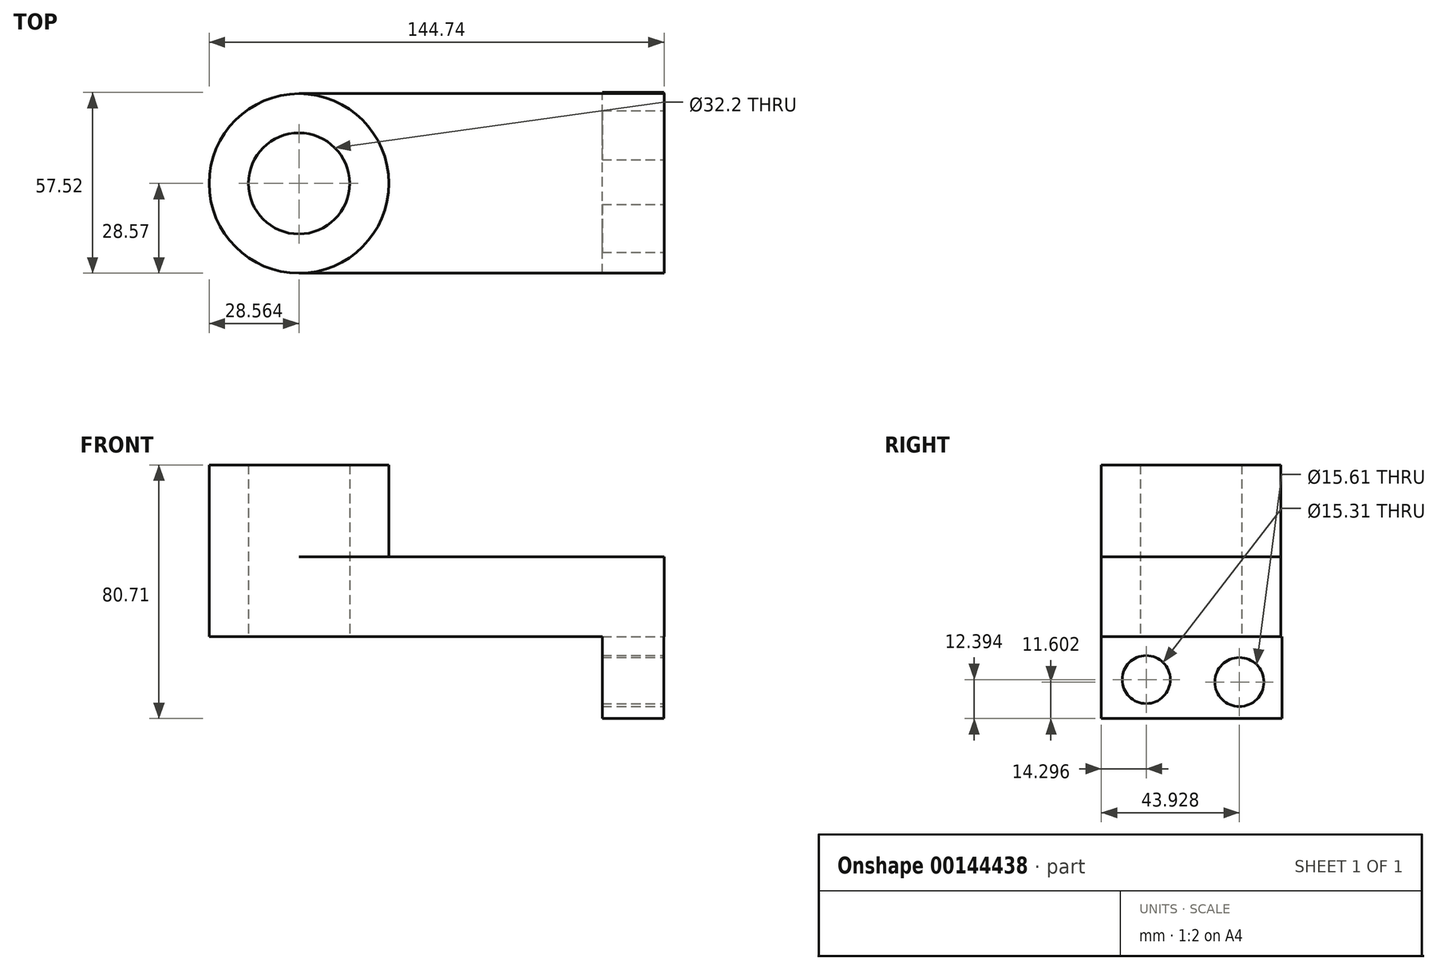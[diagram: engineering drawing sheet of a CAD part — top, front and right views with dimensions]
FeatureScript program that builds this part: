
annotation { "Feature Type Name" : "Feature", "Feature Type Description" : "" }
export const myFeature = defineFeature(function(context is Context, id is Id, definition is map)
    precondition{}
    {
        {
            var Q0;
            Q0=qCreatedBy(makeId("Top.planeOp"),FACE);
            var sketch = newSketch(context, id + "F0", { "sketchPlane" : qUnion([Q0])});
            skLineSegment(sketch, "E0.bottom", {"start": v(-58.09, 28.57) * mm, "end": v(58.09, 28.57) * mm});
            skLineSegment(sketch, "E0.top", {"start": v(-58.09, -28.57) * mm, "end": v(58.09, -28.57) * mm});
            skLineSegment(sketch, "E0.left", {"start": v(-58.09, 28.57) * mm, "end": v(-58.09, -28.57) * mm});
            skLineSegment(sketch, "E0.right", {"start": v(58.09, 28.57) * mm, "end": v(58.09, -28.57) * mm});
            skPoint(sketch, "E0.middle", {"position": v(0, 0) * mm});
            skCircle(sketch, "E1", {"center": v(-58.09, 0) * mm, "radius": 28.57 * mm});
            skCircle(sketch, "E2", {"center": v(-58.09, 0) * mm, "radius": 16.1 * mm});
            skSolve(sketch);
        }
        {
            var Q0;
            {var subQ1=sQuery(id+"F0.wireOp",EDGE,"E0.left");var subQ3=sQuery(id+"F0.wireOp",EDGE,"E2");var subQ4=makeQuery(id+"F0.imprint","INTERSECT",VERTEX,{"disambiguationData":[OD(0.0)],"derivedFrom":[subQ1,subQ3]});Q0=makeQuery(id+"F0.imprint","IMPRINT",FACE,{"disambiguationData":[TD([[makeQuery(id+"F0.imprint","IMPRINT",EDGE,{"disambiguationData":[TD([[subQ4,-1.0]])],"derivedFrom":subQ3}),-1.0]])]});}
            var Q1;
            {var subQ1=sQuery(id+"F0.wireOp",EDGE,"E0.left");var subQ3=sQuery(id+"F0.wireOp",EDGE,"E2");var subQ4=makeQuery(id+"F0.imprint","INTERSECT",VERTEX,{"disambiguationData":[OD(0.0)],"derivedFrom":[subQ1,subQ3]});Q1=makeQuery(id+"F0.imprint","IMPRINT",FACE,{"disambiguationData":[TD([[makeQuery(id+"F0.imprint","IMPRINT",EDGE,{"disambiguationData":[TD([[subQ4,1.0]])],"derivedFrom":subQ3}),-1.0]])]});}
            var Q2;
            {var subQ0=sQuery(id+"F0.wireOp",EDGE,"E0.bottom");Q2=makeQuery(id+"F0.imprint","IMPRINT",FACE,{"disambiguationData":[TD([[makeQuery(id+"F0.imprint","IMPRINT",EDGE,{"derivedFrom":subQ0}),-1.0]])]});}
            extrude(context, id + "F1", {"entities" : qUnion([Q0, Q1, Q2]), "depth" : 25.4 * mm});
        }
        {
            var Q0;
            {var subQ1=sQuery(id+"F0.wireOp",EDGE,"E0.left");var subQ3=sQuery(id+"F0.wireOp",EDGE,"E2");var subQ4=makeQuery(id+"F0.imprint","INTERSECT",VERTEX,{"disambiguationData":[OD(0.0)],"derivedFrom":[subQ1,subQ3]});Q0=makeQuery(id+"F0.imprint","IMPRINT",FACE,{"disambiguationData":[TD([[makeQuery(id+"F0.imprint","IMPRINT",EDGE,{"disambiguationData":[TD([[subQ4,1.0]])],"derivedFrom":subQ3}),-1.0]])]});}
            var Q1;
            {var subQ1=sQuery(id+"F0.wireOp",EDGE,"E0.left");var subQ3=sQuery(id+"F0.wireOp",EDGE,"E2");var subQ4=makeQuery(id+"F0.imprint","INTERSECT",VERTEX,{"disambiguationData":[OD(0.0)],"derivedFrom":[subQ1,subQ3]});Q1=makeQuery(id+"F0.imprint","IMPRINT",FACE,{"disambiguationData":[TD([[makeQuery(id+"F0.imprint","IMPRINT",EDGE,{"disambiguationData":[TD([[subQ4,-1.0]])],"derivedFrom":subQ3}),-1.0]])]});}
            extrude(context, id + "F2", {"entities" : qUnion([Q0, Q1]), "operationType" : NewBodyOperationType.ADD, "depth" : 54.6 * mm});
        }
        {
            var Q0;
            {var subQ0=sQuery(id+"F0.wireOp",EDGE,"E0.bottom");Q0=makeQuery(id+"F0.imprint","IMPRINT",FACE,{"disambiguationData":[TD([[makeQuery(id+"F0.imprint","IMPRINT",EDGE,{"derivedFrom":subQ0}),-1.0]])]});}
            var sketch = newSketch(context, id + "F3", { "sketchPlane" : qUnion([Q0])});
            skLineSegment(sketch, "E3.bottom", {"start": v(57.98, -28.57) * mm, "end": v(38.43, -28.57) * mm});
            skLineSegment(sketch, "E3.top", {"start": v(57.98, 28.95) * mm, "end": v(38.43, 28.95) * mm});
            skLineSegment(sketch, "E3.left", {"start": v(57.98, -28.57) * mm, "end": v(57.98, 28.95) * mm});
            skLineSegment(sketch, "E3.right", {"start": v(38.43, -28.57) * mm, "end": v(38.43, 28.95) * mm});
            skSolve(sketch);
        }
        {
            var Q0;
            Q0 = qSketchRegion(id + "F3", true);
            extrude(context, id + "F4", {"entities" : qUnion([Q0]), "operationType" : NewBodyOperationType.ADD, "oppositeDirection" : true, "depth" : 26.1 * mm});
        }
        {
            var Q0;
            Q0=makeQuery(id+"F4.opExtrude","SWEPT_FACE",FACE,{"disambiguationData":[OSD([sQuery(id+"F3.wireOp",EDGE,"E3.left")])]});
            var sketch = newSketch(context, id + "F5", { "sketchPlane" : qUnion([Q0])});
            skCircle(sketch, "E4", {"center": v(-14.27, -13.7) * mm, "radius": 7.65 * mm});
            skCircle(sketch, "E5", {"center": v(15.36, -14.5) * mm, "radius": 7.8 * mm});
            skSolve(sketch);
        }
        {
            var Q0;
            Q0 = qSketchRegion(id + "F5", true);
            extrude(context, id + "F6", {"entities" : qUnion([Q0]), "operationType" : NewBodyOperationType.REMOVE, "oppositeDirection" : true, "depth" : 25.4 * mm});
        }
    });
